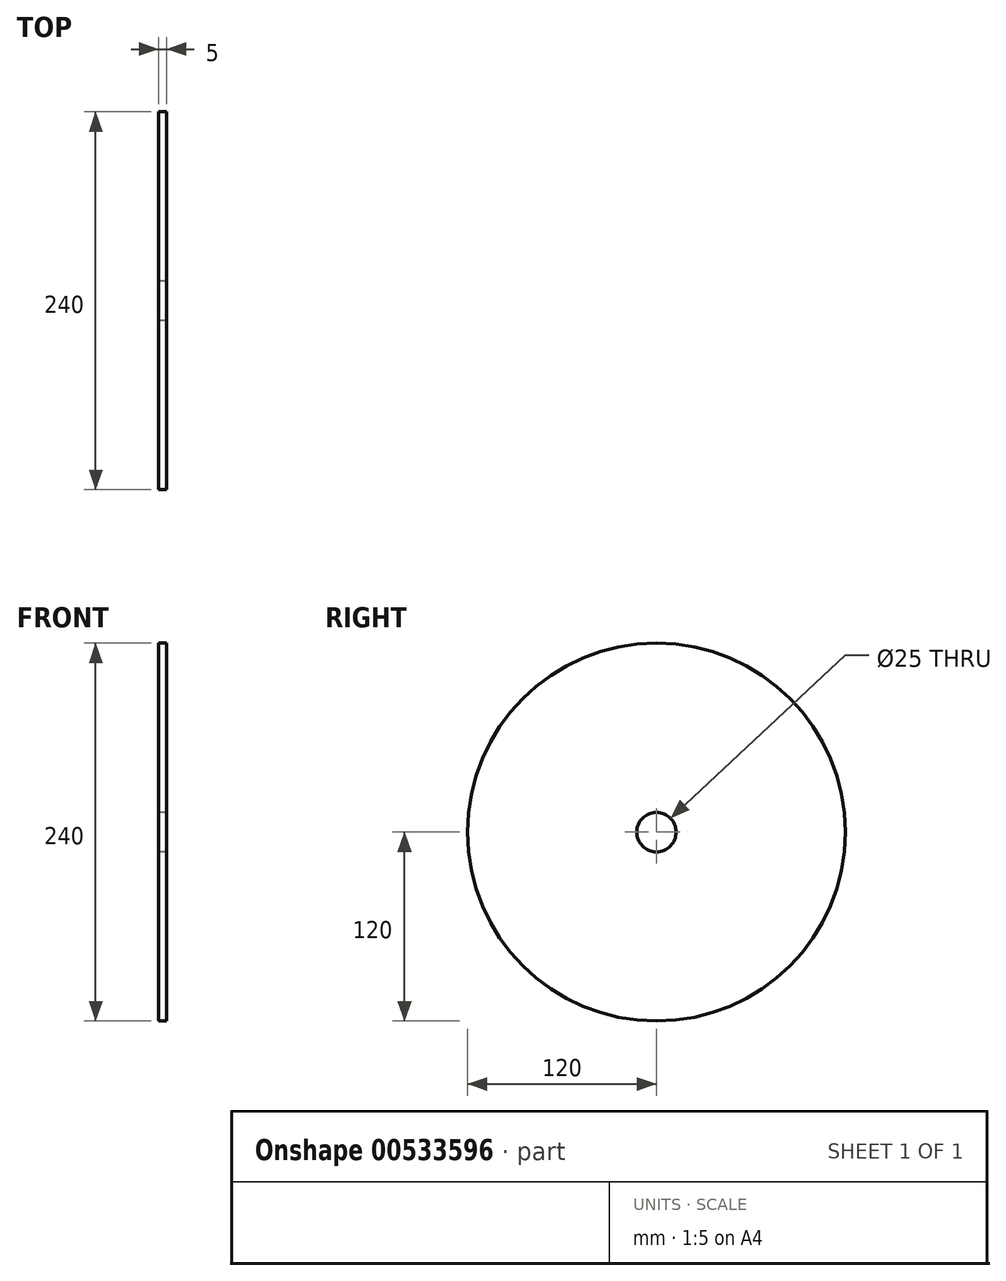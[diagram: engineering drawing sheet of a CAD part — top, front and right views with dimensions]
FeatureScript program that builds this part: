
annotation { "Feature Type Name" : "Feature", "Feature Type Description" : "" }
export const myFeature = defineFeature(function(context is Context, id is Id, definition is map)
    precondition{}
    {
        {
            var Q0;
            Q0=qCreatedBy(makeId("Right.planeOp"),FACE);
            var sketch = newSketch(context, id + "F0", { "sketchPlane" : qUnion([Q0])});
            skCircle(sketch, "E0", {"center": v(0, 0) * mm, "radius": 120 * mm});
            skCircle(sketch, "E1", {"center": v(0, 0) * mm, "radius": 12.5 * mm});
            skSolve(sketch);
        }
        {
            var Q0;
            Q0=qSketchRegion(id+"F0",true);
            extrude(context, id + "F1", {"entities" : qUnion([Q0]), "depth" : 5 * mm});
        }
    });
